# Revit family: Bath-Apron-Kohler-K_1283
name_source: partatom
category: Specialty Equipment
revit_build: Autodesk Revit 2015 (Build: 20140606_1530(x64)
units: mm (PartAtom-declared; Revit-internal decimal feet)

## types (5) — shared parameters
ADA Compliant = No
Assembly Code = D2010510
Default Elevation = 0' - 0"
Height = 1' - 6 1/2"
Keynote = 10 28 00
Length = 6' - 0"
Manufacturer = Kohler
Material = Acrylic
Product Documentation Link = https://www.us.kohler.com
Product Name = Removable Apron, 6' x 18-1/2''
Product Page URL = http://www.us.kohler.com
URL = http://www.us.kohler.com
Version = 2014 - v1.0a
Width = 0' - 2 1/4"

## per-type parameters (varying)
| type | ControlM | Description | Finish | Model |
| 0-White | 0 | 6' Removable Apron, White | Acrylic - Kohler - 0 - White | K-1283-0 |
| 47-Almond | 47 | 6' Removable Apron, Almond | Acrylic - Kohler - 47 - Almond | K-1283-47 |
| 96-Biscuit | 96 | 6' Removable Apron, Biscuit | Acrylic - Kohler - 96 - Biscuit | K-1283-96 |
| G9-Sandbar | 79 | 6' Removable Apron, Sandbar | Acrylic - Kohler - G9 - Sandbar | K-1283-G9 |
| NY-Dune | 1425 | 6' Removable Apron, Dune | Acrylic - Kohler - NY - Dune | K-1283-NY |

## geometry (parser evidence)
native form markers: Extrusion x6, Sweep x6
no freeform markers — native parametric forms only
